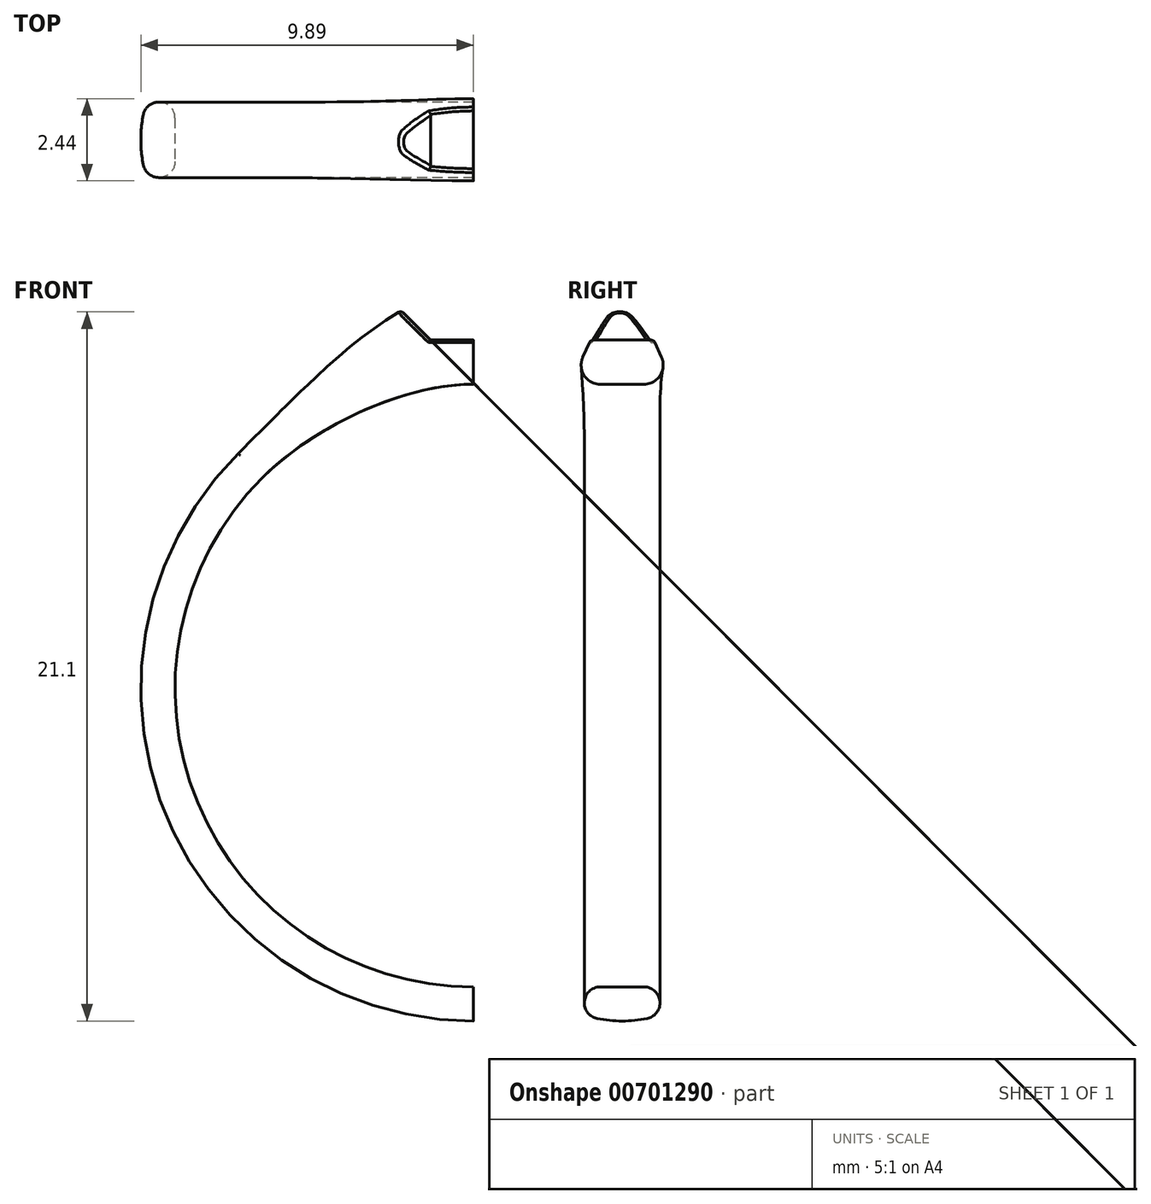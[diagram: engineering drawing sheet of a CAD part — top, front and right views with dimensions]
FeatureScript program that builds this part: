
annotation { "Feature Type Name" : "Feature", "Feature Type Description" : "" }
export const myFeature = defineFeature(function(context is Context, id is Id, definition is map)
    precondition{}
    {
        {
            var Q0;
            Q0=qCreatedBy(makeId("Right.planeOp"),FACE);
            var sketch = newSketch(context, id + "F0", { "sketchPlane" : qUnion([Q0])});
            skCircle(sketch, "E0", {"center": v(-0.65, -9.35) * mm, "radius": 0.48 * mm});
            skCircle(sketch, "E1", {"center": v(0.65, -9.35) * mm, "radius": 0.48 * mm});
            skCircle(sketch, "E2", {"center": v(0, -6.08) * mm, "radius": 3.81 * mm, "construction": true});
            skLineSegment(sketch, "E3", {"start": v(-0.65, -8.88) * mm, "end": v(0.65, -8.88) * mm});
            skArc(sketch, "E4", {"start": v(-0.74, -9.82) * mm, "mid": v(0, -9.9) * mm, "end": v(0.74, -9.82) * mm});
            skLineSegment(sketch, "E5", {"start": v(-3.81, 0) * mm, "end": v(3.81, 0) * mm, "construction": true});
            skSolve(sketch);
        }
        {
            var Q0;
            Q0 = qSketchRegion(id + "F0", true);
            var Q1;
            Q1=sQuery(id+"F0.wireOp",EDGE,"E5");
            revolve(context, id + "F1", {"entities" : qUnion([Q0]), "axis" : qUnion([Q1]), "revolveType" : RevolveType.ONE_DIRECTION, "angle" : 135 * degree});
        }
        {
            var Q0;
            Q0=makeQuery(id+"F1.opRevolve","CAP_FACE",FACE,{"disambiguationData":[OSD([sQuery(id+"F0.wireOp",EDGE,"E0"),sQuery(id+"F0.wireOp",EDGE,"E1"),sQuery(id+"F0.wireOp",EDGE,"E3"),sQuery(id+"F0.wireOp",EDGE,"E4")])],"isStart":true});
            var sketch = newSketch(context, id + "F2", { "sketchPlane" : qUnion([Q0])});
            skLineSegment(sketch, "E6", {"start": v(-0.65, 9.06) * mm, "end": v(0.65, 9.06) * mm});
            skArc(sketch, "E7", {"start": v(-1.17, 9.86) * mm, "mid": v(-1.13, 9.32) * mm, "end": v(-0.65, 9.06) * mm});
            skArc(sketch, "E8", {"start": v(0.65, 9.06) * mm, "mid": v(1.13, 9.32) * mm, "end": v(1.17, 9.86) * mm});
            skArc(sketch, "E9", {"start": v(0.35, 11.69) * mm, "mid": v(0, 11.91) * mm, "end": v(-0.35, 11.69) * mm});
            skLineSegment(sketch, "E10", {"start": v(-0.35, 11.69) * mm, "end": v(-1.17, 9.86) * mm});
            skLineSegment(sketch, "E11", {"start": v(0.35, 11.69) * mm, "end": v(1.17, 9.86) * mm});
            skSolve(sketch);
        }
        {
            var Q1;
            Q1=makeQuery(id+"F1.opRevolve","CAP_FACE",FACE,{"disambiguationData":[OSD([sQuery(id+"F0.wireOp",EDGE,"E0"),sQuery(id+"F0.wireOp",EDGE,"E1"),sQuery(id+"F0.wireOp",EDGE,"E3"),sQuery(id+"F0.wireOp",EDGE,"E4")])],"isStart":false});
            var Q2;
            Q2=makeQuery(id+"F2.imprint","IMPRINT",FACE,{"disambiguationData":[TD([[makeQuery(id+"F2.imprint","IMPRINT",EDGE,{"derivedFrom":sQuery(id+"F2.wireOp",EDGE,"E6")}),1.0]])]});
            var Q3;
            Q3=makeQuery(id+"F1.opRevolve","CAP_EDGE",EDGE,{"disambiguationData":[OSD([sQuery(id+"F0.wireOp",EDGE,"E4")])],"isStart":false});
            var Q4;
            Q4=sQuery(id+"F2.wireOp",EDGE,"E9");
            loft(context, id + "F3", {"operationType" : NewBodyOperationType.ADD, "startCondition" : LoftEndDerivativeType.NORMAL_TO_PROFILE, "startMagnitude" : 1, "endCondition" : LoftEndDerivativeType.NORMAL_TO_PROFILE, "endMagnitude" : 1, "sheetProfilesArray" : [{ "sheetProfileEntities" : qUnion([Q1]) }, { "sheetProfileEntities" : qUnion([Q2]) }], "guidesArray" : [{ "guideEntities" : qUnion([Q3]), "guideDerivativeType" : LoftGuideDerivativeType.DEFAULT, "guideDerivativeMagnitude" : 1 }, { "guideEntities" : qUnion([Q4]), "guideDerivativeType" : LoftGuideDerivativeType.DEFAULT, "guideDerivativeMagnitude" : 1 }]});
        }
        {
            var Q0;
            Q0=qCreatedBy(makeId("Front.planeOp"),FACE);
            var sketch = newSketch(context, id + "F4", { "sketchPlane" : qUnion([Q0])});
            skFitSpline(sketch, "E12.0", {"points": [v(0, 9.86) * mm, v(0, 10.47) * mm, v(0, 11.08) * mm, v(0, 11.69) * mm]});
            skLineSegment(sketch, "E13", {"start": v(0, 10.37) * mm, "end": v(-1.27, 10.37) * mm});
            skLineSegment(sketch, "E14", {"start": v(-1.27, 10.37) * mm, "end": v(-2.29, 11.38) * mm});
            skLineSegment(sketch, "E15", {"start": v(-2.29, 11.38) * mm, "end": v(0, 12.45) * mm});
            skLineSegment(sketch, "E16", {"start": v(0, 12.45) * mm, "end": v(0, 11.69) * mm});
            skSolve(sketch);
        }
        {
            var Q0;
            Q0 = qSketchRegion(id + "F4", true);
            extrude(context, id + "F5", {"entities" : qUnion([Q0]), "operationType" : NewBodyOperationType.REMOVE, "endBound" : BoundingType.SYMMETRIC, "oppositeDirection" : true, "depth" : 25.4 * mm, "offsetDistance" : 25.4 * mm});
        }
        {
            var Q0;
            Q0=makeQuery(id+"F5.boolean.opBoolean","INTERSECT",EDGE,{"disambiguationData":[OD(1.0)],"derivedFrom":[makeQuery(id+"F3.opLoft","SWEPT_FACE",FACE,{"disambiguationData":[OSD([sQuery(id+"F0.wireOp",EDGE,"E0"),sQuery(id+"F0.wireOp",EDGE,"E3"),sQuery(id+"F2.wireOp",EDGE,"E6"),sQuery(id+"F2.wireOp",EDGE,"E7"),sQuery(id+"F2.wireOp",EDGE,"E8")])]}),makeQuery(id+"F5.opExtrude","SWEPT_FACE",FACE,{"disambiguationData":[OSD([sQuery(id+"F4.wireOp",EDGE,"E13")])]})]});
            var Q1;
            Q1=makeQuery(id+"F5.boolean.opBoolean","INTERSECT",EDGE,{"derivedFrom":[makeQuery(id+"F3.opLoft","SWEPT_FACE",FACE,{"disambiguationData":[OSD([sQuery(id+"F0.wireOp",EDGE,"E0"),sQuery(id+"F0.wireOp",EDGE,"E3"),sQuery(id+"F2.wireOp",EDGE,"E6"),sQuery(id+"F2.wireOp",EDGE,"E7"),sQuery(id+"F2.wireOp",EDGE,"E8")])]}),makeQuery(id+"F5.opExtrude","SWEPT_FACE",FACE,{"disambiguationData":[OSD([sQuery(id+"F4.wireOp",EDGE,"E14")])]})]});
            var Q2;
            Q2=makeQuery(id+"F5.boolean.opBoolean","INTERSECT",EDGE,{"disambiguationData":[OD(0.0)],"derivedFrom":[makeQuery(id+"F3.opLoft","SWEPT_FACE",FACE,{"disambiguationData":[OSD([sQuery(id+"F0.wireOp",EDGE,"E0"),sQuery(id+"F0.wireOp",EDGE,"E3"),sQuery(id+"F2.wireOp",EDGE,"E6"),sQuery(id+"F2.wireOp",EDGE,"E7"),sQuery(id+"F2.wireOp",EDGE,"E8")])]}),makeQuery(id+"F5.opExtrude","SWEPT_FACE",FACE,{"disambiguationData":[OSD([sQuery(id+"F4.wireOp",EDGE,"E13")])]})]});
            fillet(context, id + "F6", {"entities" : qUnion([Q0, Q1, Q2]), "radius" : 0.13 * mm, "tangentPropagation" : true, "allowEdgeOverflow" : false});
        }
        {
            var Q0;
            Q0=qCreatedBy(makeId("Front.planeOp"),FACE);
            var sketch = newSketch(context, id + "F7", { "sketchPlane" : qUnion([Q0])});
            skPoint(sketch, "E17.0", {"position": v(0, 9.32) * mm});
            skPoint(sketch, "E18.0", {"position": v(0, -8.88) * mm});
            skLineSegment(sketch, "E19", {"start": v(0, 9.32) * mm, "end": v(0, -8.88) * mm, "construction": true});
            skSolve(sketch);
        }
    });
